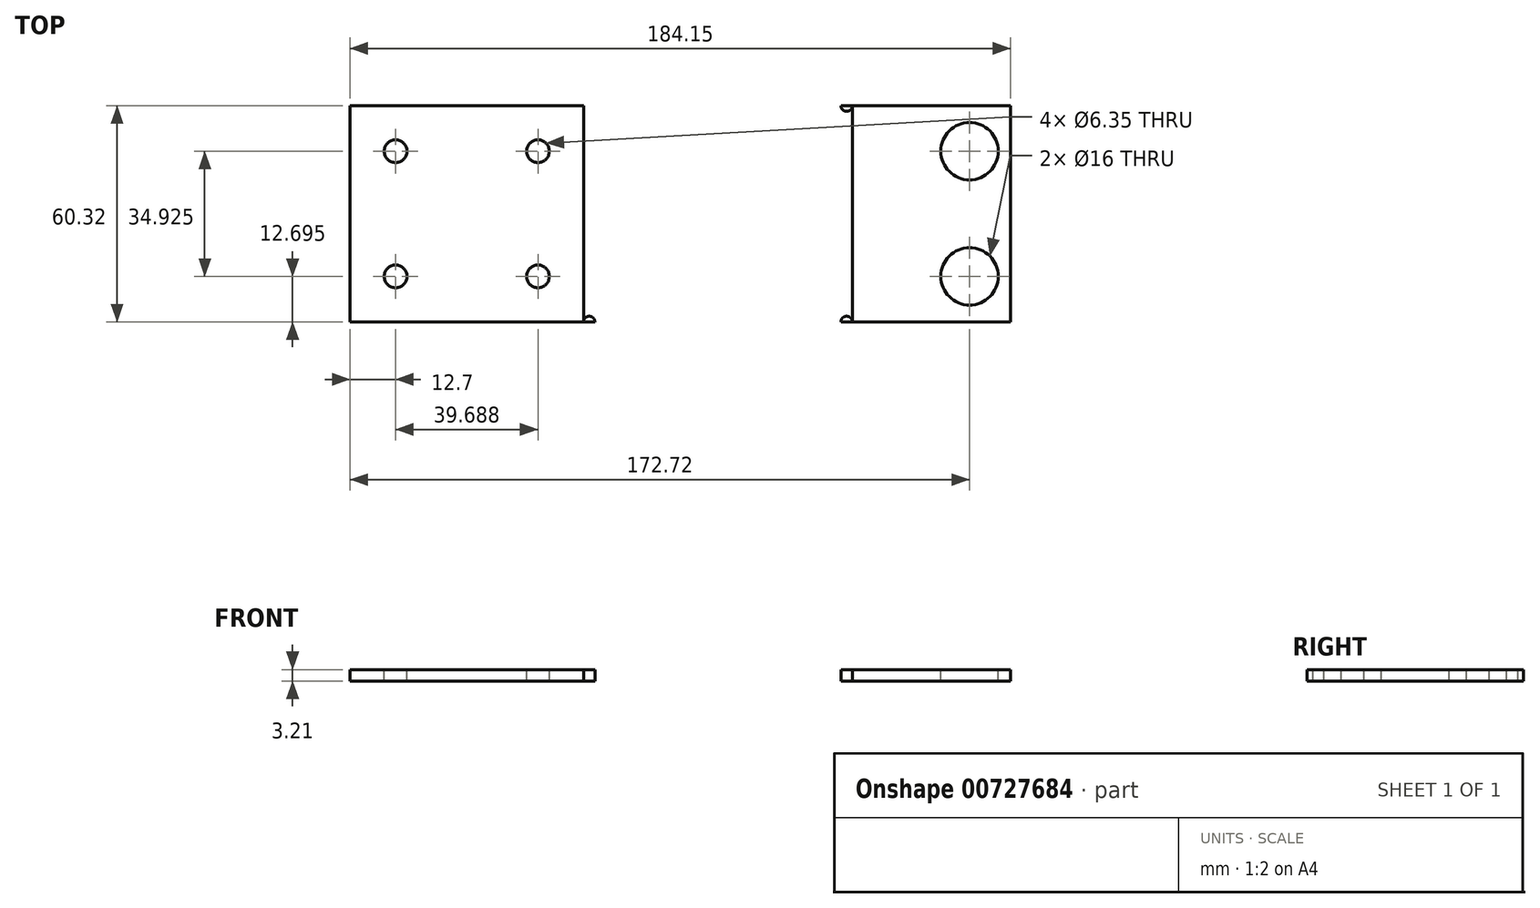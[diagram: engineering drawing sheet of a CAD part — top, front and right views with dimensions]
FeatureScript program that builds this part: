
annotation { "Feature Type Name" : "Feature", "Feature Type Description" : "" }
export const myFeature = defineFeature(function(context is Context, id is Id, definition is map)
    precondition{}
    {
        {
            var Q0;
            Q0=qCreatedBy(makeId("Front.planeOp"),FACE);
            var sketch = newSketch(context, id + "F0", { "sketchPlane" : qUnion([Q0])});
            skLineSegment(sketch, "E0.bottom", {"start": v(-69.85, 3.18) * mm, "end": v(-4.76, 3.18) * mm});
            skLineSegment(sketch, "E0.top", {"start": v(-69.85, 0) * mm, "end": v(-4.76, 0) * mm});
            skLineSegment(sketch, "E0.left", {"start": v(-69.85, 3.18) * mm, "end": v(-69.85, 0) * mm});
            skLineSegment(sketch, "E0.right", {"start": v(0, 0) * mm, "end": v(0, 0) * mm});
            skLineSegment(sketch, "E1.right", {"start": v(114.3, 3.15) * mm, "end": v(114.3, -0.03) * mm});
            skLineSegment(sketch, "E2", {"start": v(70.17, -0.03) * mm, "end": v(114.3, -0.03) * mm});
            skLineSegment(sketch, "E3", {"start": v(70.17, 3.15) * mm, "end": v(114.3, 3.15) * mm});
            skPoint(sketch, "E4.visualSharp", {"position": v(68.58, -0.03) * mm});
            skPoint(sketch, "E5.visualSharp", {"position": v(0, 0) * mm});
            skLineSegment(sketch, "E6", {"start": v(-4.76, 3.18) * mm, "end": v(70.17, 3.15) * mm});
            skLineSegment(sketch, "E7", {"start": v(-4.76, 0) * mm, "end": v(70.17, -0.03) * mm});
            skSolve(sketch);
        }
        {
            var Q0;
            Q0=makeQuery(id+"F0.imprint","IMPRINT",FACE,{"disambiguationData":[TD([[makeQuery(id+"F0.imprint","IMPRINT",EDGE,{"derivedFrom":sQuery(id+"F0.wireOp",EDGE,"E0.bottom")}),-1.0]])]});
            extrude(context, id + "F1", {"entities" : qUnion([Q0]), "depth" : 60.32 * mm, "offsetDistance" : 25.4 * mm});
        }
        {
            var Q0;
            Q0=makeQuery(id+"F1.opExtrude","SWEPT_FACE",FACE,{"disambiguationData":[OSD([sQuery(id+"F0.wireOp",EDGE,"E3")])]});
            var sketch = newSketch(context, id + "F2", { "sketchPlane" : qUnion([Q0])});
            skCircle(sketch, "E8", {"center": v(102.87, -12.7) * mm, "radius": 8 * mm});
            skCircle(sketch, "E9", {"center": v(102.87, -47.63) * mm, "radius": 8 * mm});
            skSolve(sketch);
        }
        {
            var Q0;
            Q0=qSketchRegion(id+"F2",true);
            extrude(context, id + "F3", {"entities" : qUnion([Q0]), "operationType" : NewBodyOperationType.REMOVE, "oppositeDirection" : true, "depth" : 25.4 * mm, "offsetDistance" : 25.4 * mm});
        }
        {
            var Q0;
            Q0=makeQuery(id+"F1.opExtrude","SWEPT_FACE",FACE,{"disambiguationData":[OSD([sQuery(id+"F0.wireOp",EDGE,"E0.bottom")])]});
            var sketch = newSketch(context, id + "F4", { "sketchPlane" : qUnion([Q0])});
            skCircle(sketch, "E10", {"center": v(-57.15, -12.7) * mm, "radius": 3.18 * mm});
            skCircle(sketch, "E11", {"center": v(-57.15, -47.62) * mm, "radius": 3.18 * mm});
            skSolve(sketch);
        }
        {
            var Q0;
            Q0=makeQuery(id+"F4.imprint","IMPRINT",FACE,{"disambiguationData":[TD([[makeQuery(id+"F4.imprint","IMPRINT",EDGE,{"derivedFrom":sQuery(id+"F4.wireOp",EDGE,"E10")}),1.0]])]});
            var Q1;
            Q1=makeQuery(id+"F4.imprint","IMPRINT",FACE,{"disambiguationData":[TD([[makeQuery(id+"F4.imprint","IMPRINT",EDGE,{"derivedFrom":sQuery(id+"F4.wireOp",EDGE,"E10")}),1.0]])]});
            var Q2;
            Q2=makeQuery(id+"F4.imprint","IMPRINT",FACE,{"disambiguationData":[TD([[makeQuery(id+"F4.imprint","IMPRINT",EDGE,{"derivedFrom":sQuery(id+"F4.wireOp",EDGE,"E11")}),1.0]])]});
            var Q3;
            Q3=makeQuery(id+"F4.imprint","IMPRINT",FACE,{"disambiguationData":[TD([[makeQuery(id+"F4.imprint","IMPRINT",EDGE,{"derivedFrom":sQuery(id+"F4.wireOp",EDGE,"E11")}),1.0]])]});
            var Q4;
            Q4=sQuery(id+"F4.wireOp",EDGE,"E10");
            var Q5;
            Q5=sQuery(id+"F4.wireOp",EDGE,"E10");
            var Q6;
            Q6=sQuery(id+"F4.wireOp",EDGE,"E11");
            var Q7;
            Q7=sQuery(id+"F4.wireOp",EDGE,"E11");
            extrude(context, id + "F5", {"entities" : qUnion([Q0, Q1, Q2, Q3]), "operationType" : NewBodyOperationType.REMOVE, "surfaceEntities" : qUnion([Q4, Q5, Q6, Q7]), "oppositeDirection" : true, "depth" : 25.4 * mm, "offsetDistance" : 25.4 * mm});
        }
        {
            var Q0;
            Q0=makeQuery(id+"F1.opExtrude","SWEPT_FACE",FACE,{"disambiguationData":[OSD([sQuery(id+"F0.wireOp",EDGE,"E0.bottom")])]});
            var sketch = newSketch(context, id + "F6", { "sketchPlane" : qUnion([Q0])});
            skCircle(sketch, "E12", {"center": v(-17.46, -12.7) * mm, "radius": 3.18 * mm});
            skCircle(sketch, "E13", {"center": v(-17.46, -47.62) * mm, "radius": 3.18 * mm});
            skSolve(sketch);
        }
        {
            var Q0;
            Q0=makeQuery(id+"F6.imprint","IMPRINT",FACE,{"disambiguationData":[TD([[makeQuery(id+"F6.imprint","IMPRINT",EDGE,{"derivedFrom":sQuery(id+"F6.wireOp",EDGE,"E12")}),1.0]])]});
            var Q1;
            Q1=makeQuery(id+"F6.imprint","IMPRINT",FACE,{"disambiguationData":[TD([[makeQuery(id+"F6.imprint","IMPRINT",EDGE,{"derivedFrom":sQuery(id+"F6.wireOp",EDGE,"E13")}),1.0]])]});
            var Q2;
            Q2=sQuery(id+"F6.wireOp",EDGE,"E12");
            var Q3;
            Q3=sQuery(id+"F6.wireOp",EDGE,"E13");
            extrude(context, id + "F7", {"entities" : qUnion([Q0, Q1]), "operationType" : NewBodyOperationType.REMOVE, "surfaceEntities" : qUnion([Q2, Q3]), "oppositeDirection" : true, "depth" : 25.4 * mm, "offsetDistance" : 25.4 * mm});
        }
        {
            var Q0;
            Q0=makeQuery(id+"F1.opExtrude","SWEPT_FACE",FACE,{"disambiguationData":[OSD([sQuery(id+"F0.wireOp",EDGE,"E6")])]});
            var sketch = newSketch(context, id + "F8", { "sketchPlane" : qUnion([Q0])});
            skArc(sketch, "E14", {"start": v(-4.76, 0) * mm, "mid": v(-3.18, -1.59) * mm, "end": v(-1.59, 0) * mm});
            skArc(sketch, "E15", {"start": v(70.17, 0) * mm, "mid": v(68.58, -1.59) * mm, "end": v(67, 0) * mm});
            skArc(sketch, "E16", {"start": v(-4.76, -60.33) * mm, "mid": v(-3.18, -58.74) * mm, "end": v(-1.59, -60.33) * mm});
            skArc(sketch, "E17", {"start": v(67, -60.32) * mm, "mid": v(68.58, -58.74) * mm, "end": v(70.17, -60.33) * mm});
            skLineSegment(sketch, "E18", {"start": v(-4.76, -60.33) * mm, "end": v(-1.59, -60.33) * mm});
            skLineSegment(sketch, "E19", {"start": v(67, -60.33) * mm, "end": v(70.17, -60.33) * mm});
            skLineSegment(sketch, "E20", {"start": v(67, 0) * mm, "end": v(70.17, 0) * mm});
            skLineSegment(sketch, "E21", {"start": v(-4.76, 0) * mm, "end": v(-1.59, 0) * mm});
            skSolve(sketch);
        }
        {
            var Q0;
            Q0=makeQuery(id+"F8.imprint","IMPRINT",FACE,{"disambiguationData":[TD([[makeQuery(id+"F8.imprint","IMPRINT",EDGE,{"derivedFrom":sQuery(id+"F8.wireOp",EDGE,"E16")}),-1.0]])]});
            var Q1;
            Q1=makeQuery(id+"F8.imprint","IMPRINT",FACE,{"disambiguationData":[TD([[makeQuery(id+"F8.imprint","IMPRINT",EDGE,{"derivedFrom":sQuery(id+"F8.wireOp",EDGE,"E17")}),-1.0]])]});
            var Q2;
            Q2=makeQuery(id+"F8.imprint","IMPRINT",FACE,{"disambiguationData":[TD([[makeQuery(id+"F8.imprint","IMPRINT",EDGE,{"derivedFrom":sQuery(id+"F8.wireOp",EDGE,"E15")}),-1.0]])]});
            var Q3;
            Q3=makeQuery(id+"F8.imprint","IMPRINT",FACE,{"disambiguationData":[TD([[makeQuery(id+"F8.imprint","IMPRINT",EDGE,{"derivedFrom":sQuery(id+"F8.wireOp",EDGE,"E14")}),1.0]])]});
            var Q4;
            Q4=sQuery(id+"F8.wireOp",EDGE,"E14");
            var Q5;
            Q5=sQuery(id+"F8.wireOp",EDGE,"E15");
            var Q6;
            Q6=sQuery(id+"F8.wireOp",EDGE,"E16");
            var Q7;
            Q7=sQuery(id+"F8.wireOp",EDGE,"E17");
            extrude(context, id + "F9", {"entities" : qUnion([Q0, Q1, Q2, Q3]), "operationType" : NewBodyOperationType.REMOVE, "surfaceEntities" : qUnion([Q4, Q5, Q6, Q7]), "oppositeDirection" : true, "depth" : 25.4 * mm, "offsetDistance" : 25.4 * mm});
        }
    });
